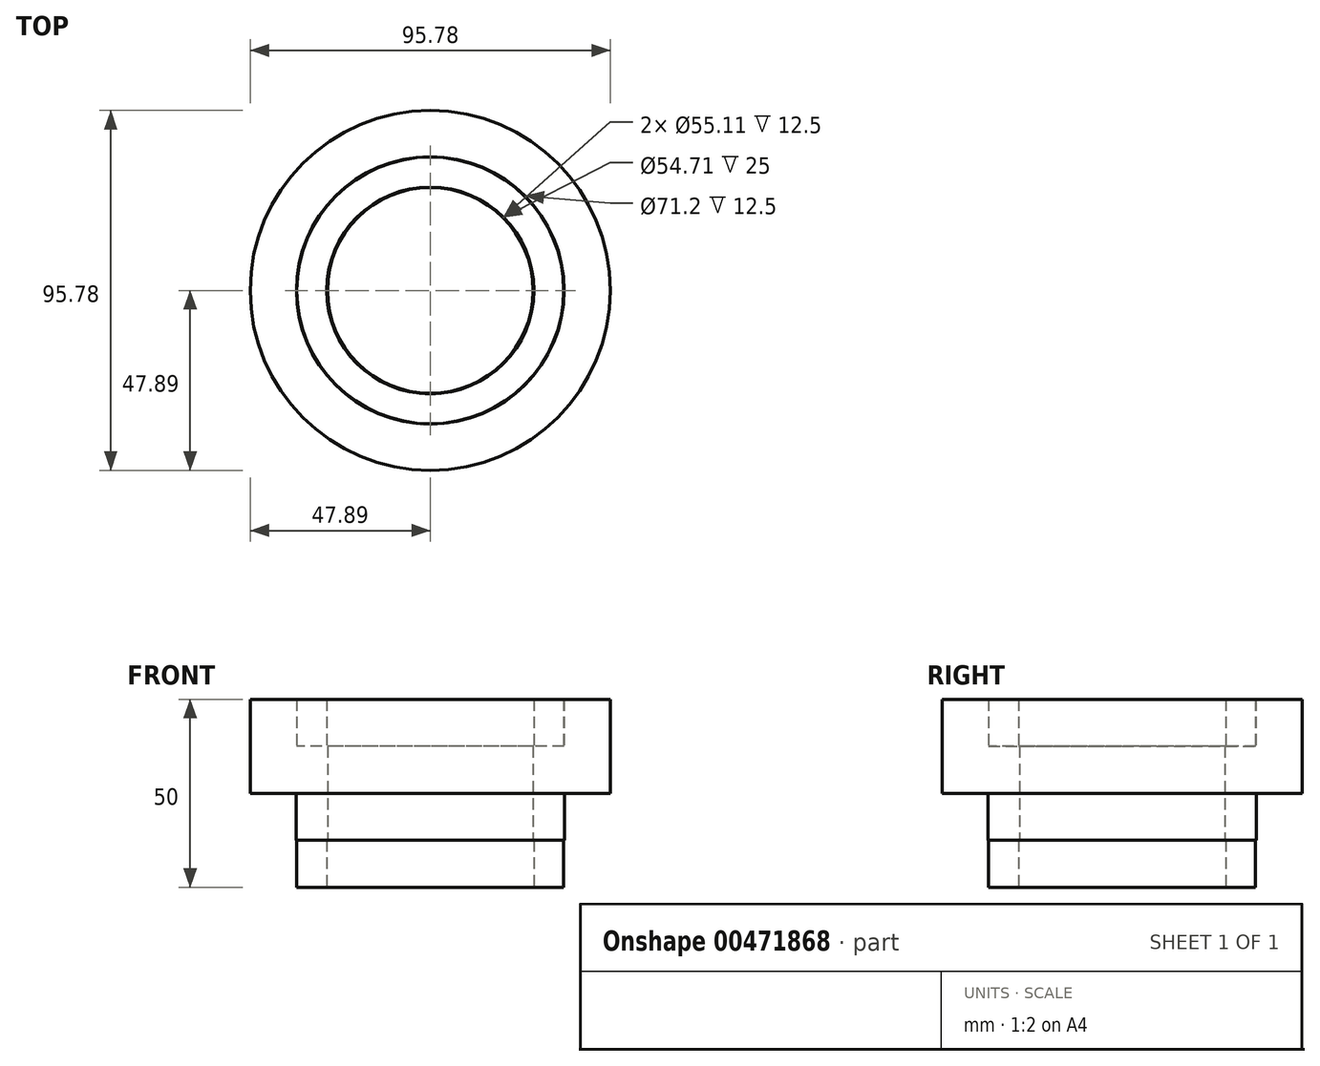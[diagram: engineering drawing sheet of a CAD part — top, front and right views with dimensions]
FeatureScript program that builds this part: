
annotation { "Feature Type Name" : "Feature", "Feature Type Description" : "" }
export const myFeature = defineFeature(function(context is Context, id is Id, definition is map)
    precondition{}
    {
        {
            var Q0;
            Q0=qCreatedBy(makeId("Top.planeOp"),FACE);
            var sketch = newSketch(context, id + "F0", { "sketchPlane" : qUnion([Q0])});
            skCircle(sketch, "E0", {"center": v(0, 0) * mm, "radius": 47.83 * mm});
            skCircle(sketch, "E1", {"center": v(0, 0) * mm, "radius": 27.35 * mm});
            skSolve(sketch);
        }
        {
            var Q0;
            Q0 = qSketchRegion(id + "F0", true);
            extrude(context, id + "F1", {"entities" : qUnion([Q0]), "endBound" : BoundingType.SYMMETRIC, "depth" : 25 * mm});
        }
        {
            var Q0;
            Q0=qCreatedBy(makeId("Top.planeOp"),FACE);
            var sketch = newSketch(context, id + "F2", { "sketchPlane" : qUnion([Q0])});
            skCircle(sketch, "E2", {"center": v(0, 0) * mm, "radius": 27.56 * mm});
            skCircle(sketch, "E3", {"center": v(0, 0) * mm, "radius": 35.5 * mm});
            skSolve(sketch);
        }
        {
            var Q0;
            Q0 = qSketchRegion(id + "F2", true);
            extrude(context, id + "F3", {"entities" : qUnion([Q0]), "operationType" : NewBodyOperationType.ADD, "endBound" : BoundingType.SYMMETRIC, "depth" : 50 * mm});
        }
        {
            var Q0;
            Q0=qCreatedBy(makeId("Top.planeOp"),FACE);
            var sketch = newSketch(context, id + "F4", { "sketchPlane" : qUnion([Q0])});
            skCircle(sketch, "E4", {"center": v(0, 0) * mm, "radius": 35.25 * mm});
            skCircle(sketch, "E5", {"center": v(0, 0) * mm, "radius": 47.7 * mm});
            skSolve(sketch);
        }
        {
            var Q0;
            Q0 = qSketchRegion(id + "F4", true);
            extrude(context, id + "F5", {"entities" : qUnion([Q0]), "operationType" : NewBodyOperationType.ADD, "endBound" : BoundingType.SYMMETRIC, "depth" : 25 * mm});
        }
        {
            var Q0;
            Q0=qCreatedBy(makeId("Top.planeOp"),FACE);
            var sketch = newSketch(context, id + "F6", { "sketchPlane" : qUnion([Q0])});
            skCircle(sketch, "E6", {"center": v(0, 0) * mm, "radius": 35.71 * mm});
            skCircle(sketch, "E7", {"center": v(0, 0) * mm, "radius": 48.08 * mm});
            skSolve(sketch);
        }
        {
            var Q0;
            Q0 = qSketchRegion(id + "F6", true);
            extrude(context, id + "F7", {"entities" : qUnion([Q0]), "operationType" : NewBodyOperationType.REMOVE, "oppositeDirection" : true, "depth" : 25 * mm});
        }
        {
            var Q0;
            Q0=qCreatedBy(makeId("Top.planeOp"),FACE);
            var sketch = newSketch(context, id + "F8", { "sketchPlane" : qUnion([Q0])});
            skCircle(sketch, "E8", {"center": v(0, 0) * mm, "radius": 35.6 * mm});
            skCircle(sketch, "E9", {"center": v(0, 0) * mm, "radius": 47.9 * mm});
            skSolve(sketch);
        }
        {
            var Q0;
            Q0 = qSketchRegion(id + "F8", true);
            extrude(context, id + "F9", {"entities" : qUnion([Q0]), "operationType" : NewBodyOperationType.ADD, "depth" : 25 * mm});
        }
    });
